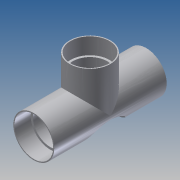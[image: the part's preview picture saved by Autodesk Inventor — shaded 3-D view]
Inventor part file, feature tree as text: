
AUTODESK INVENTOR PART (.ipt)
format: ipt  version: 2014 SP1 (Build 180222100, 222)  size: 199,168 bytes
history: native  units: in
note: dims shown in document units (in); Inventor stores cm internally (conversion verified against a paired STEP export)
features: sketch x10, extrude x8, plane x2
ambient origin geometry x8: Origin, YZ Plane, XZ Plane, XY Plane, X Axis, Y Axis, Z Axis, Center Point
bodies: Solid1 (feature_tree)
feature tree (20):
  extrude  "mainBody"  Depth=6.875in TaperAngle=0.0deg
  sketch  "Sketch10"  dims[d29=3.4375in d30=2.5in]
  plane  "Work Plane5"
  extrude  "TBody"  Depth=2.5in
  extrude  "TSocket"  Depth=1.25in
  extrude  "TTube"  Depth=2.1in
  extrude  "mainTube"  Depth=2.1in
  extrude  "mainSocket1"  Depth=2.375in
  extrude  "mainSocket2"  Depth=2.375in
  sketch  "Sketch23"  dims[d68=1.1022in]
  plane  "Work Plane9"
  extrude  "Extrusion18"  Depth=2.0in
  sketch  "Sketch1"  dims[d0=2.5in d1=6.875in d2=0.0in]
  sketch  "Sketch11"  dims[d31=1.5in d32=1.25in d33=0.0in d34=0.0in d35=2.375in]
  sketch  "Sketch12"  dims[d37=1.0in d38=0.0in d39=2.1in]
  sketch  "Sketch13"  dims[d41=1.5in d42=0.0in d43=2.1in]
  sketch  "Sketch14"  dims[d45=7.0in d46=0.0in d47=2.375in]
  sketch  "Sketch15"  dims[d49=1.0in d50=0.0in d51=2.375in]
  sketch  "Sketch16"  dims[d53=1.0in d54=0.0in d67=2.0in]
  sketch  "Sketch24"  dims[d69=1.2in d70=2.9in d71=8.0in d72=0.0in]
